# Revit family: Basin-Drop In-Caroma Centro Vanity1
name_source: partatom
category: Plumbing Fixtures
revit_build: Autodesk Revit Architecture 2012 (Build: 20110916_2132(x64)
units: mm (PartAtom-declared; Revit-internal decimal feet)

## types (1)
- Centro - 3 Tap Holes
    1 Taphole = No
    3 Tapholes = Yes
    Assembly Code = D2010310
    CW Connection = No
    Cost = 165 $
    Default Elevation = 0 mm  [stored 0 ft]
    Description = Centro Vanity Basin
    HW Connection = No
    Keynote = HB
    Manufacturer = Caroma
    Material_ANZRS = Porcelain-White-Caroma
    Model = 664135W
    PlumbingMaterial_ANZRS = PVC-White-Caroma
    Spout Penetration = 0 mm  [stored 0 ft]
    Tap Penetrations = 0 mm  [stored 0 ft]
    Type Comments = Capacity: 4.55L to overflow, Overflow available only, White plug and chrome flush fitting waste included
    URL = www.caroma.com.au
    Vent Connection = No
    WFU = 2
    Waste = Metal-Chrome-Caroma
    Waste Connection = Yes

note: [stored X ft] marks values corroborated as IEEE doubles in the binary element streams (Revit-internal decimal feet)

## geometry (parser evidence)
native form markers: Blend x2, Sweep x2
no freeform markers — native parametric forms only
